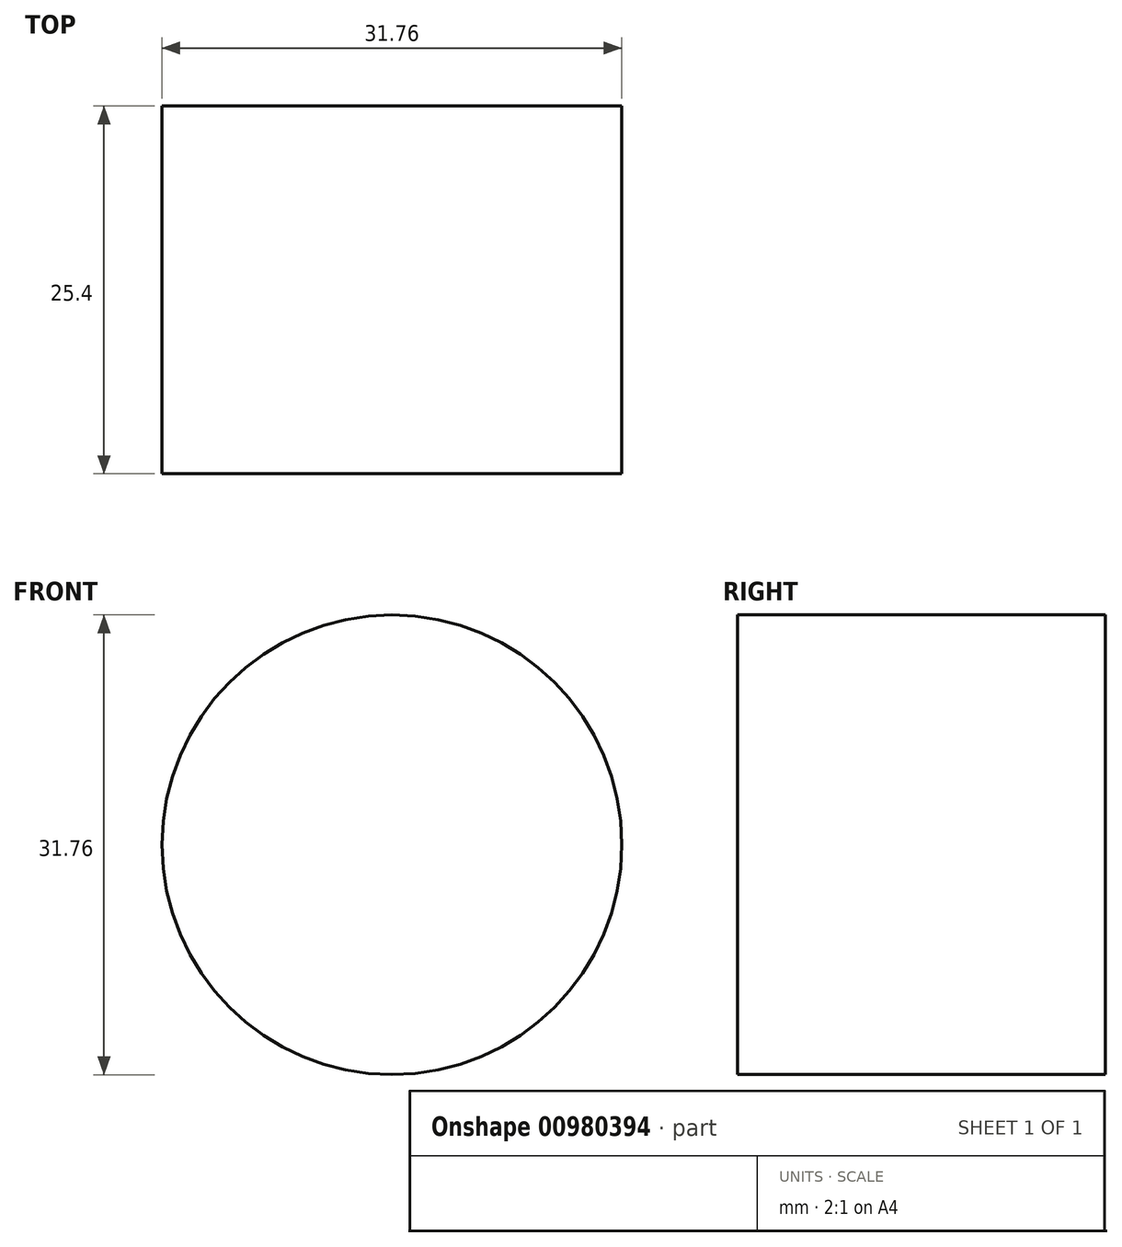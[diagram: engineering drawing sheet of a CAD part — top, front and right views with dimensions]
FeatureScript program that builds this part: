
annotation { "Feature Type Name" : "Feature", "Feature Type Description" : "" }
export const myFeature = defineFeature(function(context is Context, id is Id, definition is map)
    precondition{}
    {
        {
            var Q0;
            Q0=qCreatedBy(makeId("Front.planeOp"),FACE);
            var sketch = newSketch(context, id + "F0", { "sketchPlane" : qUnion([Q0])});
            skCircle(sketch, "E0", {"center": v(0, 0) * mm, "radius": 15.88 * mm});
            skSolve(sketch);
        }
        {
            var Q0;
            Q0 = qSketchRegion(id + "F0", true);
            extrude(context, id + "F1", {"entities" : qUnion([Q0]), "endBound" : BoundingType.SYMMETRIC, "depth" : 25.4 * mm, "offsetDistance" : 25.4 * mm});
        }
    });
